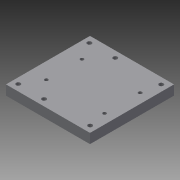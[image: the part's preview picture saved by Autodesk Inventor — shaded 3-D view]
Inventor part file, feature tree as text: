
AUTODESK INVENTOR PART (.ipt)
format: ipt  version: 2015 SP1 (Build 190203100, 203)  size: 105,472 bytes
history: native  units: in
note: dims shown in document units (in); Inventor stores cm internally (conversion verified against a paired STEP export)
features: sketch x3, hole x2, extrude x1, projected_geometry x1
ambient origin geometry x8: Origin, YZ Plane, XZ Plane, XY Plane, X Axis, Y Axis, Z Axis, Center Point
bodies: Solid1 (feature_tree)
feature tree (7):
  extrude  "Extrusion1"  Depth=6.5in
  hole  "Hole1"  [1 undecoded]
  hole  "Hole2"  [1 undecoded]
  sketch  "Sketch2"  dims[d0=6.5in d1=6.5in]
  sketch  "Sketch3"  dims[d2=0.75in d3=0.0in d4=0.45in]
  sketch  "Sketch4"  dims[d5=2.0in d6=3.56in d7=0.5in d8=0.332in d9=0.75in d10=0.635in d11=0.25in d12=0.5635in d13=1.0in d14=0.8108in d15=1.253in d16=4.5in d17=1.872in d18=0.266in d19=0.75in d20=0.507in d21=0.25in d22=0.5635in d23=1.0in d24=0.8108in]
  projected_geometry  "Projected Loop1"
note: 2 required parameter values undecoded (feature->parameter linkage not recoverable at this tier; creation-order binding heuristic only, values carry confidence <= 0.55)
